# Revit family: NBS_TapcoRoofingProducts_DryFxngAbtmnts_Tapco_AbutmentVentilator
name_source: partatom
category: Generic Models
units: mm (PartAtom-declared; Revit-internal decimal feet)

## family parameters
Can host rebar = No
Cut with Voids When Loaded = No
Part Type = Normal
Room Calculation Point = No
Round Connector Dimension = Use Diameter
Shared = No

## types (1)
- Tapco_AbutmentVentilator
    AbutmentVentilatorMaterial = NBS_TapcoRoofingProducts_Acrylonitrilebutadienestyrene(ABS)_Black
    Applications = Suitable and recommended for all Tapco Roofing products, can be used in conjunction with traditional ‘lead roll’ details on slate and shake roofs, particularly suitable for Tapco Slate Classic tiles
    AssetType = Fixed
    BIMObjectName = NBS_TapcoRoofingProducts_DryFixingAbutments_Tapco_AbutmentVentilator
    Category = Pr_35_90_93_27:Dry fixing abutments
    CodePerformance = BS 5250
    Color = Black
    Combustible = Yes
    Description = Abutment Ventilator providing unobtrusive high-level ventilation in conjunction with lead roll details on slate and shake roofs
    DurationUnit = year
    ExpectedLife = 25+ years
    Features = Guaranteed 5000 mm²/m ventilation provision to comply with BS 5250 and Building Regulations, deluge and driving rain resistant as well as preventing large insect ingress, unobtrusive when installed. Hidden within the roof flashings, can be used with AluFlash, the lead-free alternative, each unit overlaps the next to ensure integrity of flashing, quick and easy to install. Does not affect the normal laying of the roof covering
    Finish = Polymeric resin
    IfcExportAs = IfcCoveringType
    IfcExportType = ROOFING
    IsExternal = Yes
    ManufacturerName = Tapco Roofing Products
    ManufacturerURL = www.tapcoroofingproducts.com
    Material = Acrylonitrile butadiene styrene (ABS)
    ModelReference = Tapco_AbutmentVentilator
    NBSCertification = www.nationalbimlibrary.com/cert/mabbzcmc
    NBSDescription = Dry fixing abutments
    NBSReference = 45-80-90/372
    Name = DryFixingAbutments_Tapco_AbutmentVentilator_TapcoRoofingProducts
    NominalHeight = 24 mm  [stored 0.0787402 ft]
    NominalLength = 1035 mm  [stored 3.39567 ft]
    NominalWidth = 203 mm  [stored 0.66601 ft]
    Pitch = Suitable for pitches of 20° and above
    ProductInformation = https://www.tapcoroofingproducts.com
    Shape = Rectangular
    Size = 1035 x 203 mm
    Status = UNSET
    ThermalTransmittance = 0
    Uniclass2015Code = Pr_35_90_93_27
    Uniclass2015Title = Dry fixing abutments
    Uniclass2015Version = Products v1.20
    VentilatorHeight = 24 mm  [stored 0.0787402 ft]
    VentilatorWidth = 203 mm  [stored 0.66601 ft]
    Version = 1
    WarrantyDescription = 40-years
    WarrantyDurationUnit = year

note: [stored X ft] marks values corroborated as IEEE doubles in the binary element streams (Revit-internal decimal feet)

## geometry (parser evidence)
native form markers: Sweep x2
no freeform markers — native parametric forms only
